# Revit family: Lighting_Fixture-Procedure-Midmark-Ritter-255-Ceiling_Mounted-Single
name_source: partatom
category: Lighting Fixtures
revit_build: Autodesk Revit 2016 (Build: 20170117_1200(x64)
units: mm (PartAtom-declared; Revit-internal decimal feet)

## family parameters
Cut with Voids When Loaded = No
Host = Face
Light Source = No
OmniClass Number = 23.80.70.11.17
OmniClass Title = Specialized Lighting by Location or Use
Part Type = Normal
Room Calculation Point = No
Round Connector Dimension = Use Diameter
Shared = No

## types (4) — shared parameters
Amps = 1 A
Assembly Code = D5020200
Ballast Material = Metal-Midmark-Aluminum
Connector Description = Connector for Electrical Power
Default Elevation = 4' - 0"
Description = Single Mount Minor Procedure Light
Fixture Finish = Plastic-Midmark-White
Lamp = 16 LEDs arranged in 4x4 array
Lens Material = Glass-Midmark-Lens
Load Classification = Lighting
Manufacturer = Midmark
Number of Poles = 1
Power Factor = 1
Product Documentation Link = http://www.midmark.com
Product Page URL = http://www.midmark.com
URL = www.midmark.com
Wattage Comments = 32 Watt rating

## per-type parameters (varying)
| type | 8ft | Apparent Load | Arm Height | Arm Length | Model | Voltage |
| 255-001 - 115V | Yes | 81 VA | 2' - 5 29/32" | 1' - 10" | 255-001 | 115 V |
| 255-002 - 115V | No | 81 VA | 1' - 7 3/32" | 2' - 0" | 255-002 | 115 V |
| 255-001 - 230V | Yes | 115 VA | 2' - 5 29/32" | 1' - 10" | 255-001 | 230 V |
| 255-002 - 230V | No | 115 VA | 1' - 7 3/32" | 2' - 0" | 255-002 | 230 V |

## geometry (parser evidence)
native form markers: Blend x10, Sweep x11
no freeform markers — native parametric forms only
